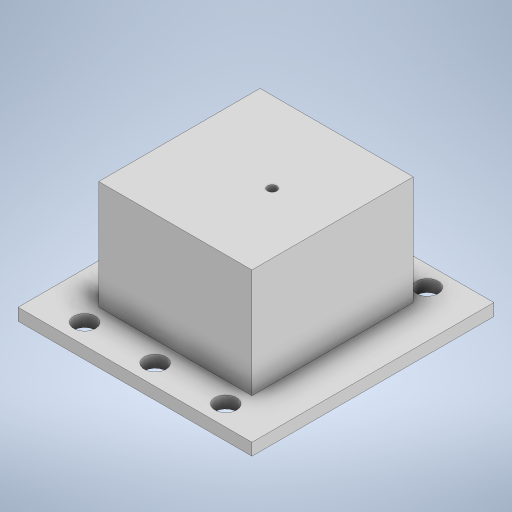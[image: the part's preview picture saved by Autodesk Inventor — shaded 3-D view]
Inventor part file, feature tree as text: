
AUTODESK INVENTOR PART (.ipt)
format: ipt  version: 2024 (Build 280153000, 153)  size: 303,104 bytes
history: native  units: mm
features: extrude x6, sketch x6, plane x3
ambient origin geometry x8: Origin, YZ Plane, XZ Plane, XY Plane, X Axis, Y Axis, Z Axis, Center Point
bodies: Body1 (feature_tree)
feature tree (15):
  plane  "Work Plane5"
  extrude  "Extrusion34"  Depth=40.0mm
  plane  "Work Plane2"
  extrude  "Extrusion35"  Depth=30.0mm
  plane  "Work Plane1"
  extrude  "Extrusion51"  Depth=30.0mm
  sketch  "Sketch77"  dims[d211=10.0mm d212=0.0mm d219=35.0mm]
  extrude  "Extrusion53"  Depth=10.0mm
  extrude  "Extrusion54"  Depth=60.0mm
  extrude  "Extrusion56"  Depth=3.0mm TaperAngle=0.0deg
  sketch  "Sketch45"  dims[d142=38.0mm d143=40.0mm]
  sketch  "Sketch47"  dims[d144=30.0mm d145=0.0mm d146=36.0mm]
  sketch  "Sketch74"  dims[d147=30.0mm d148=-2.617994mm d210=2.3mm]
  sketch  "Sketch78"  dims[d220=58.0mm d221=60.0mm]
  sketch  "Sketch81"  dims[d222=3.0mm d223=0.0mm d224=3.0mm d225=0.0mm d232=5.0mm d233=11.5mm d234=5.4mm d235=17.5mm d236=5.4mm d237=17.5mm d243=5.4mm d245=5.4mm d246=17.5mm d247=5.4mm d248=17.5mm d250=30.0mm d251=0.0mm d49=0.5mm d50=0.872665mm d51=0.5mm d52=0.872665mm d130=0.5mm d131=0.872665mm d132=0.5mm d133=0.872665mm d156=0.5mm d157=0.872665mm d158=0.5mm d159=0.872665mm d173=0.5mm d174=0.872665mm d175=0.5mm d176=0.872665mm d226=0.5mm d227=0.872665mm]
